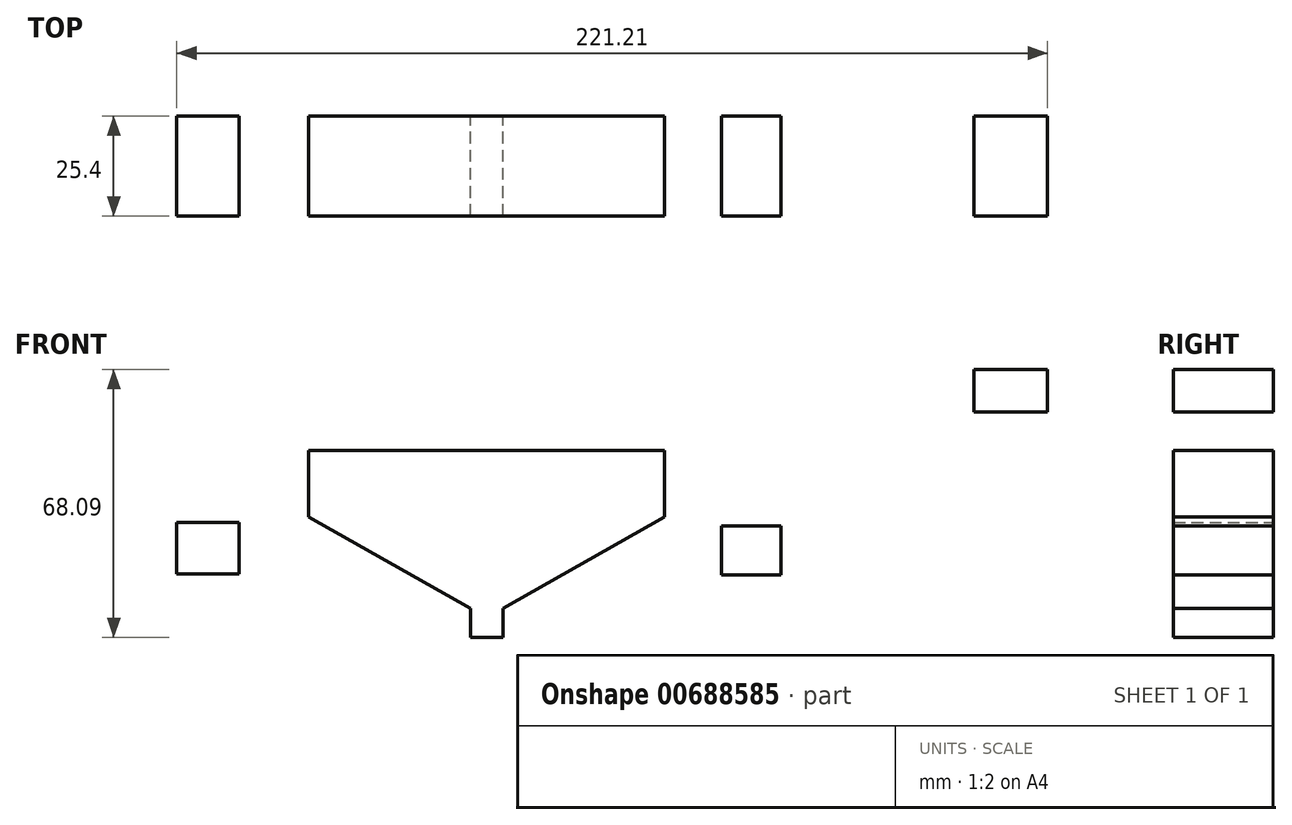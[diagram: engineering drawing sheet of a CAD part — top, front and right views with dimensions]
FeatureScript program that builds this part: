
annotation { "Feature Type Name" : "Feature", "Feature Type Description" : "" }
export const myFeature = defineFeature(function(context is Context, id is Id, definition is map)
    precondition{}
    {
        {
            var Q0;
            Q0=qCreatedBy(makeId("Front.planeOp"),FACE);
            var sketch = newSketch(context, id + "F0", { "sketchPlane" : qUnion([Q0])});
            skLineSegment(sketch, "E0.bottom", {"start": v(45.22, -8.47) * mm, "end": v(-45.22, -8.47) * mm});
            skLineSegment(sketch, "E0.top", {"start": v(45.22, 8.47) * mm, "end": v(-45.22, 8.47) * mm});
            skLineSegment(sketch, "E0.left", {"start": v(45.22, -8.47) * mm, "end": v(45.22, 8.47) * mm});
            skLineSegment(sketch, "E0.right", {"start": v(-45.22, -8.47) * mm, "end": v(-45.22, 8.47) * mm});
            skPoint(sketch, "E0.middle", {"position": v(0, 0) * mm});
            skLineSegment(sketch, "E1.bottom", {"start": v(-4.14, -29) * mm, "end": v(4.14, -29) * mm});
            skLineSegment(sketch, "E1.top", {"start": v(-4.14, -39.1) * mm, "end": v(4.14, -39.1) * mm});
            skLineSegment(sketch, "E1.left", {"start": v(-4.14, -29) * mm, "end": v(-4.14, -39.1) * mm});
            skLineSegment(sketch, "E1.right", {"start": v(4.14, -29) * mm, "end": v(4.14, -39.1) * mm});
            skPoint(sketch, "E1.middle", {"position": v(0, -34.05) * mm});
            skFitSpline(sketch, "E2", {"points": [v(0, -34.05) * mm, v(-45.22, -8.47) * mm], "startDerivative": vector(-45.22, 25.58) * mm, "endDerivative": vector(-45.22, 25.58) * mm});
            skFitSpline(sketch, "E3", {"points": [v(0, -34.05) * mm, v(45.22, -8.47) * mm], "startDerivative": vector(45.22, 25.58) * mm, "endDerivative": vector(45.22, 25.58) * mm});
            skLineSegment(sketch, "E4.bottom", {"start": v(-78.72, -22.88) * mm, "end": v(-62.87, -22.88) * mm});
            skLineSegment(sketch, "E4.top", {"start": v(-78.72, -9.9) * mm, "end": v(-62.87, -9.9) * mm});
            skLineSegment(sketch, "E4.left", {"start": v(-78.72, -22.88) * mm, "end": v(-78.72, -9.9) * mm});
            skLineSegment(sketch, "E4.right", {"start": v(-62.87, -22.88) * mm, "end": v(-62.87, -9.9) * mm});
            skPoint(sketch, "E4.middle", {"position": v(-70.8, -16.4) * mm});
            skLineSegment(sketch, "E5.bottom", {"start": v(59.63, -23.24) * mm, "end": v(74.76, -23.24) * mm});
            skLineSegment(sketch, "E5.top", {"start": v(59.63, -10.75) * mm, "end": v(74.76, -10.75) * mm});
            skLineSegment(sketch, "E5.left", {"start": v(59.63, -23.24) * mm, "end": v(59.63, -10.75) * mm});
            skLineSegment(sketch, "E5.right", {"start": v(74.76, -23.24) * mm, "end": v(74.76, -10.75) * mm});
            skPoint(sketch, "E5.middle", {"position": v(67.2, -17) * mm});
            skFitSpline(sketch, "E6", {"points": [v(-45.22, -8.47) * mm, v(-70.8, -22.88) * mm], "startDerivative": vector(-25.58, -14.41) * mm, "endDerivative": vector(-25.58, -14.41) * mm});
            skFitSpline(sketch, "E7", {"points": [v(45.22, -8.47) * mm, v(67.2, -23.24) * mm], "startDerivative": vector(21.98, -14.77) * mm, "endDerivative": vector(21.98, -14.77) * mm});
            skLineSegment(sketch, "E8.bottom", {"start": v(123.76, 18.2) * mm, "end": v(142.5, 18.2) * mm});
            skLineSegment(sketch, "E8.top", {"start": v(123.76, 29) * mm, "end": v(142.5, 29) * mm});
            skLineSegment(sketch, "E8.left", {"start": v(123.76, 18.2) * mm, "end": v(123.76, 29) * mm});
            skLineSegment(sketch, "E8.right", {"start": v(142.5, 18.2) * mm, "end": v(142.5, 29) * mm});
            skPoint(sketch, "E8.middle", {"position": v(133.13, 23.6) * mm});
            skSolve(sketch);
        }
        {
            var Q0;
            Q0 = qSketchRegion(id + "F0", true);
            extrude(context, id + "F1", {"entities" : qUnion([Q0]), "depth" : 25.4 * mm, "offsetDistance" : 25.4 * mm});
        }
    });
